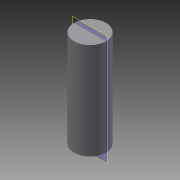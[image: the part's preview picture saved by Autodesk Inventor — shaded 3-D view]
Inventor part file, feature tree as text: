
AUTODESK INVENTOR PART (.ipt)
format: ipt  version: 2015 (Build 190159000, 159)  size: 88,576 bytes
history: native  units: mm
features: revolve x1, hole x1, sketch x1
ambient origin geometry x8: Origin, YZ Plane, XZ Plane, XY Plane, X Axis, Y Axis, Z Axis, Center Point
bodies: Solid1 (feature_tree)
feature tree (3):
  revolve  "Revolution1"  [1 undecoded]
  hole  "Hole1"  [1 undecoded]
  sketch  "Sketch1"  dims[d0=155.5mm d1=24.75mm d2=7.5mm d3=10.0mm d4=6.0mm d5=1.0mm d6=2.0mm d7=90.0deg d19=10.0mm d20=10.0mm d10=6.0mm d11=6.0mm d12=4.0mm d13=2.0mm d14=90.0deg d15=53.5mm d16=0.0mm]
note: 2 required parameter values undecoded (feature->parameter linkage not recoverable at this tier; creation-order binding heuristic only, values carry confidence <= 0.55)